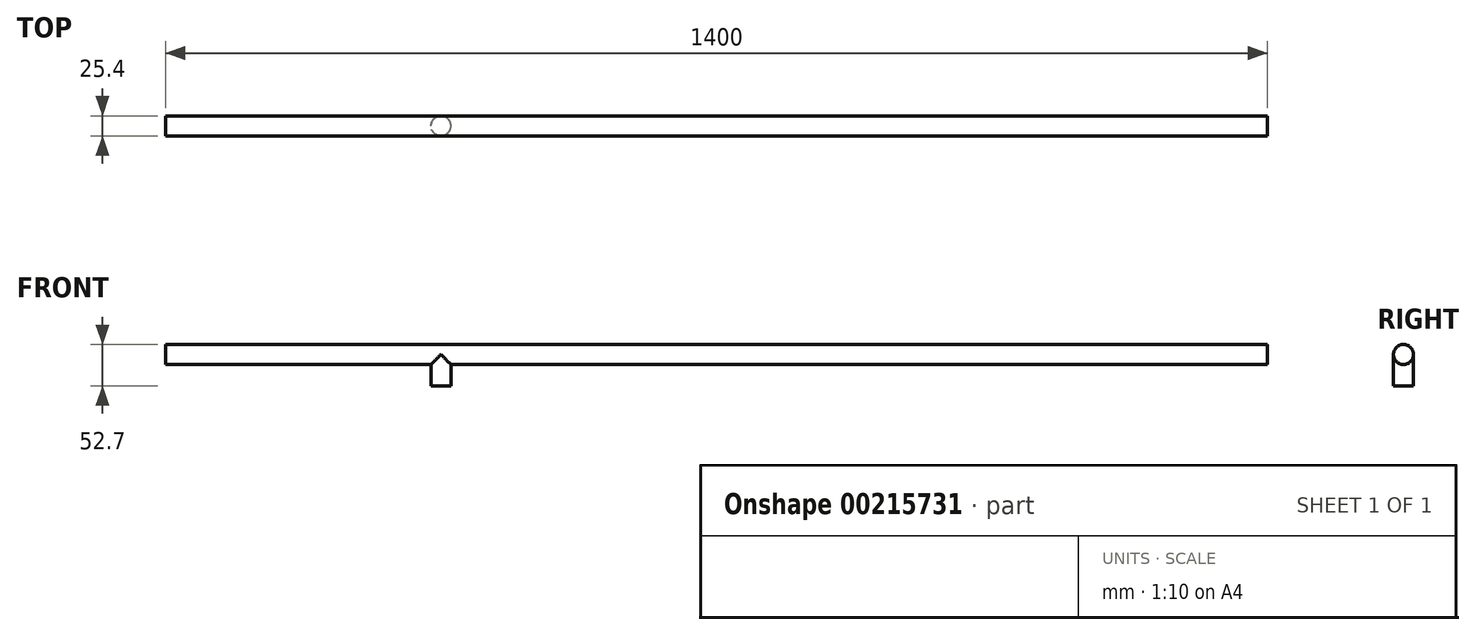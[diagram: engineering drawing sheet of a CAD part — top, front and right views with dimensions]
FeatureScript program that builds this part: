
annotation { "Feature Type Name" : "Feature", "Feature Type Description" : "" }
export const myFeature = defineFeature(function(context is Context, id is Id, definition is map)
    precondition{}
    {
        {
            var Q0;
            Q0=qCreatedBy(makeId("Right.planeOp"),FACE);
            var sketch = newSketch(context, id + "F0", { "sketchPlane" : qUnion([Q0])});
            skCircle(sketch, "E0", {"center": v(0, 0) * mm, "radius": 12.7 * mm});
            skSolve(sketch);
        }
        {
            var Q0;
            Q0=qSketchRegion(id+"F0",true);
            extrude(context, id + "F1", {"entities" : qUnion([Q0]), "oppositeDirection" : true, "depth" : 1200 * mm});
        }
        {
            var Q0;
            Q0=qCreatedBy(makeId("Top.planeOp"),FACE);
            var sketch = newSketch(context, id + "F2", { "sketchPlane" : qUnion([Q0])});
            skCircle(sketch, "E1", {"center": v(-850, 0) * mm, "radius": 12.7 * mm});
            skSolve(sketch);
        }
        {
            var Q0;
            Q0=qSketchRegion(id+"F2",true);
            extrude(context, id + "F3", {"entities" : qUnion([Q0]), "operationType" : NewBodyOperationType.ADD, "oppositeDirection" : true, "depth" : 40 * mm});
        }
        {
            var Q0;
            Q0=makeQuery(id+"F1.opExtrude","CAP_FACE",FACE,{"disambiguationData":[OSD([sQuery(id+"F0.wireOp",EDGE,"E0")])],"isStart":true});
            extrude(context, id + "F4", {"entities" : qUnion([Q0]), "operationType" : NewBodyOperationType.ADD, "depth" : 200 * mm});
        }
    });
